# Revit family: 3152400
name_source: partatom
category: Mechanical Equipment
revit_build: Autodesk Revit 2016 (Build: 20190508_0715(x64)
units: mm (PartAtom-declared; Revit-internal decimal feet)

## family parameters
Always vertical = Yes
Cut with Voids When Loaded = No
OmniClass Number = 23.75.00.00
OmniClass Title = Climate Control (HVAC)
Part Type = Normal
Room Calculation Point = No
Round Connector Dimension = Use Diameter
Shared = No
Work Plane-Based = No

## types (1)
- KRACK MICROSC 3152400
    Case Fans (MCA) = Fans
    Case Lights Amps = Lights
    Color = 701 Shadow Black
    Color - Body = 604 Mystic Grey
    Color - Bumper Rail = 701 Shadow Black
    Color - Chrome = 701 Shadow Black
    Color - End Cap = 604 Mystic Grey
    Color - End Cap Interior = 700 Interior White
    Color - Exterior Panel = 604 Mystic Grey
    Color - Interior = 700 Interior White
    Color - Legs = 701 Shadow Black
    Color - Light = Light
    Color - Shelves = 700 Interior White
    Color - Toe Kick = 701 Shadow Black
    Copper Pipes = Copper
    Copper-Liquid = Copper
    Copper-Suction = Copper
    Depth = 51.5 "
    Frequency = 60 Hz
    Glass = Glass
    Height = 58 "
    Hot Case Circuit = Hot Gas
    Length = 36.552 "
    Manufacturer = Krack Corporation
    Model = KRACK MICROSC 3152400
    Phase = 1
    Refrig. Liquid = Liquid
    Refrig. Suction = Suction
    Revit Family Dates = 08/22/22SV(052019)
    Stainless Steel = Stainless Steel
    System Control = System control
    Temp Sensor = Temp Sensor
    Toe Kick Depth = 21.125 "
    URL = www.Krack Corporation.com
    Voltage = 230 V

## geometry (parser evidence)
native form markers: Sweep x7
no freeform markers — native parametric forms only
